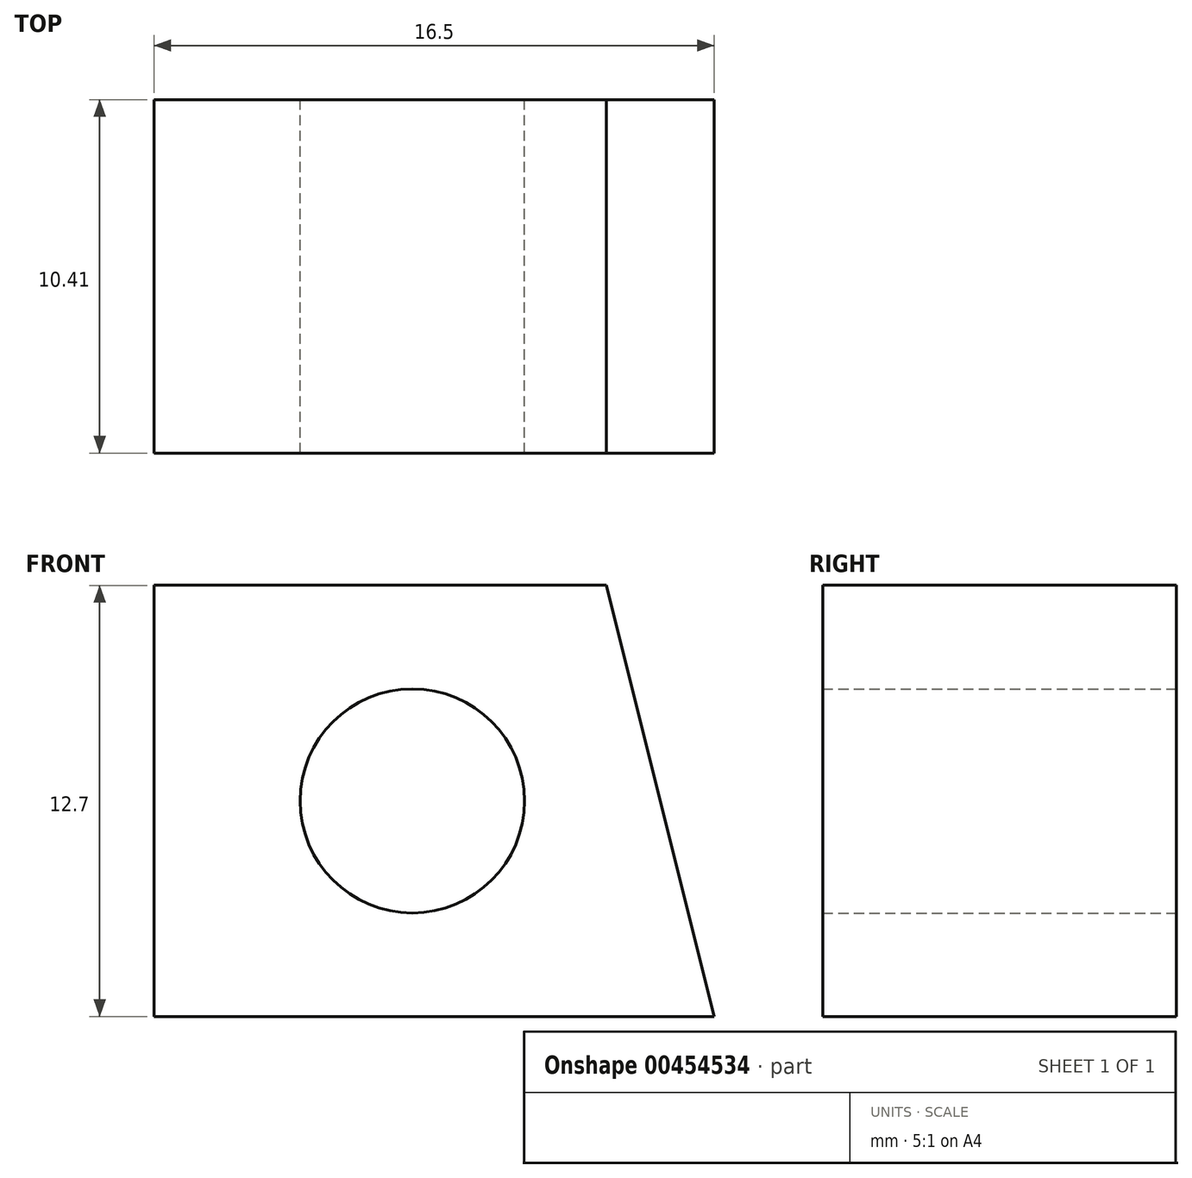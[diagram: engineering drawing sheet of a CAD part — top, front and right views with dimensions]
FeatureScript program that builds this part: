
annotation { "Feature Type Name" : "Feature", "Feature Type Description" : "" }
export const myFeature = defineFeature(function(context is Context, id is Id, definition is map)
    precondition{}
    {
        {
            var Q0;
            Q0=qCreatedBy(makeId("Front.planeOp"),FACE);
            var sketch = newSketch(context, id + "F0", { "sketchPlane" : qUnion([Q0])});
            skLineSegment(sketch, "E0", {"start": v(0, 0) * mm, "end": v(0, 6.35) * mm});
            skLineSegment(sketch, "E1", {"start": v(0, 6.35) * mm, "end": v(0, -6.35) * mm});
            skLineSegment(sketch, "E2", {"start": v(0, -6.35) * mm, "end": v(8.89, -6.35) * mm});
            skLineSegment(sketch, "E3", {"start": v(8.89, -6.35) * mm, "end": v(5.71, 6.35) * mm});
            skLineSegment(sketch, "E4", {"start": v(0, 6.35) * mm, "end": v(5.71, 6.35) * mm});
            skLineSegment(sketch, "E5", {"start": v(0, -6.35) * mm, "end": v(-7.6, -6.35) * mm});
            skLineSegment(sketch, "E6", {"start": v(-7.6, -6.35) * mm, "end": v(-7.6, 6.35) * mm});
            skLineSegment(sketch, "E7", {"start": v(-7.6, 6.35) * mm, "end": v(0, 6.35) * mm});
            skCircle(sketch, "E8", {"center": v(0, 0) * mm, "radius": 3.3 * mm});
            skSolve(sketch);
        }
        {
            var Q0;
            Q0 = qSketchRegion(id + "F0", true);
            extrude(context, id + "F1", {"entities" : qUnion([Q0]), "depth" : 10.4 * mm});
        }
    });
